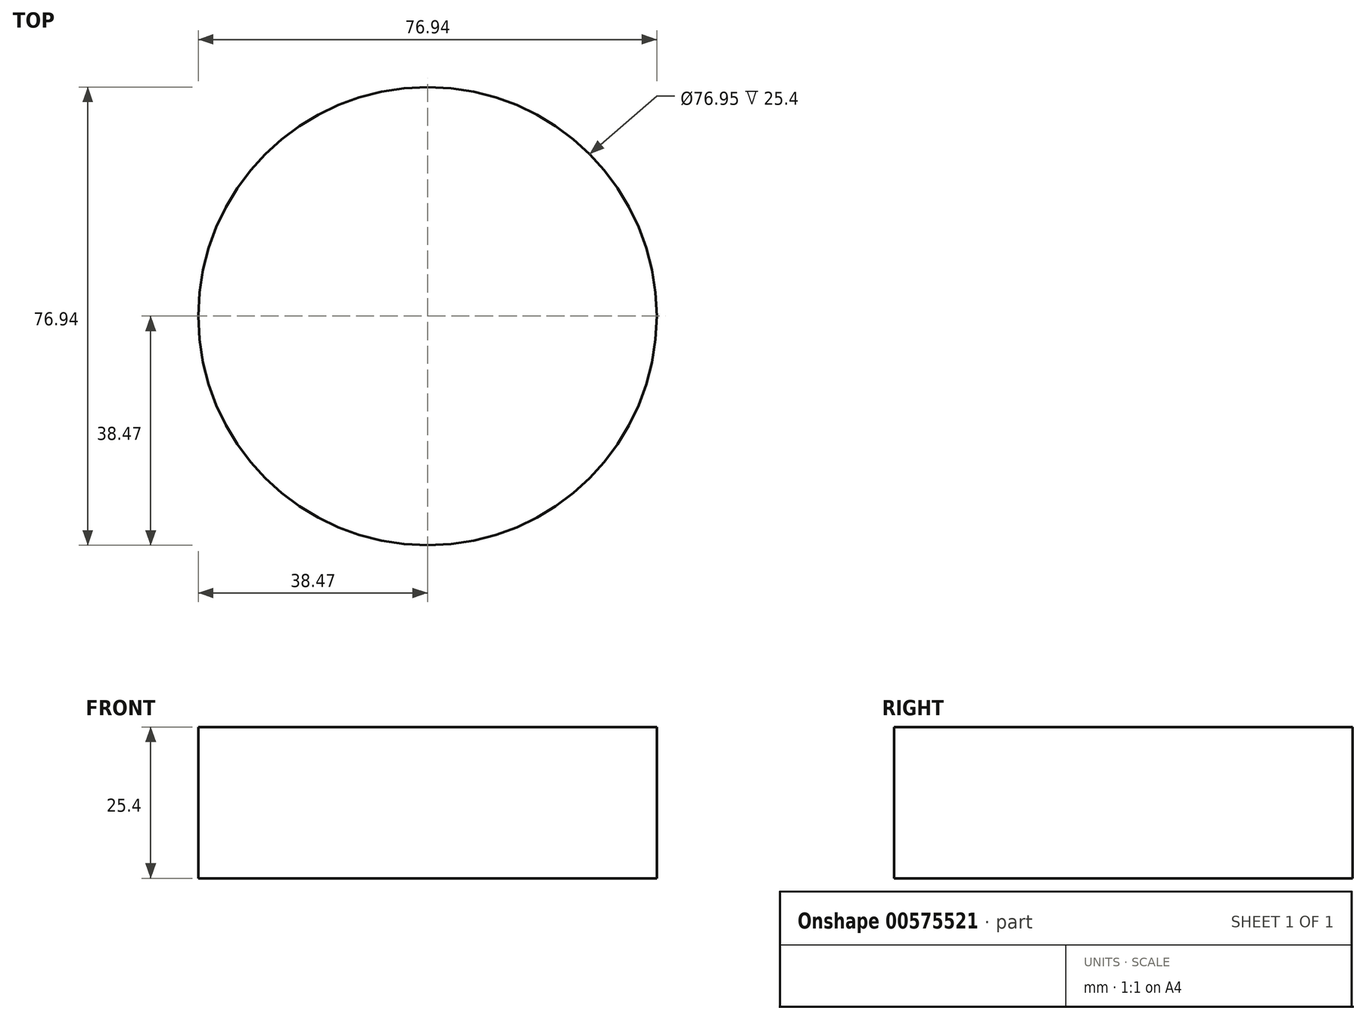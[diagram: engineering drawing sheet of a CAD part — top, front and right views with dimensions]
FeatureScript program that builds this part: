
annotation { "Feature Type Name" : "Feature", "Feature Type Description" : "" }
export const myFeature = defineFeature(function(context is Context, id is Id, definition is map)
    precondition{}
    {
        {
            var Q0;
            Q0=qCreatedBy(makeId("Top.planeOp"),FACE);
            var sketch = newSketch(context, id + "F0", { "sketchPlane" : qUnion([Q0])});
            skCircle(sketch, "E0", {"center": v(0, 0) * mm, "radius": 38.47 * mm});
            skCircle(sketch, "E1", {"center": v(0, 0) * mm, "radius": 30.38 * mm});
            skCircle(sketch, "E2", {"center": v(0, 0) * mm, "radius": 34.58 * mm});
            skSolve(sketch);
        }
        {
            var Q0;
            Q0 = qSketchRegion(id + "F0", true);
            extrude(context, id + "F1", {"entities" : qUnion([Q0]), "depth" : 25.4 * mm, "offsetDistance" : 25.4 * mm});
        }
    });
